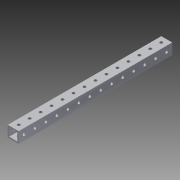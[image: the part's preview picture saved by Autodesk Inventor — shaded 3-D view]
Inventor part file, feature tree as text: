
AUTODESK INVENTOR PART (.ipt)
format: ipt  version: 2013 (Build 170138000, 138)  size: 166,912 bytes
history: native  units: in
note: dims shown in document units (in); Inventor stores cm internally (conversion verified against a paired STEP export)
features: extrude x3, sketch x3
ambient origin geometry x8: Origin, YZ Plane, XZ Plane, XY Plane, X Axis, Y Axis, Z Axis, Center Point
bodies: Solid1 (feature_tree)
feature tree (6):
  extrude  "Extrusion1"  Depth=1.0in
  extrude  "Extrusion2"  Depth=14.0in TaperAngle=0.0deg
  extrude  "Extrusion3"  Depth=0.26in
  sketch  "Sketch1"  dims[d0=1.0in d1=1.0in]
  sketch  "Sketch2"  dims[d2=0.125in d3=14.0in d4=0.0in]
  sketch  "Sketch3"  dims[d5=0.5in d7=0.26in d8=16.5in d9=0.0in d10=14.0in d11=5.5118in d13=1.0in d14=0.3937in d16=1.0in d19=0.5in d20=0.26in d21=0.26in d22=0.5in d23=0.26in d25=0.5in d26=5.5118in d28=1.0in d29=0.3937in d31=1.0in d34=1.0in d35=0.0in]
